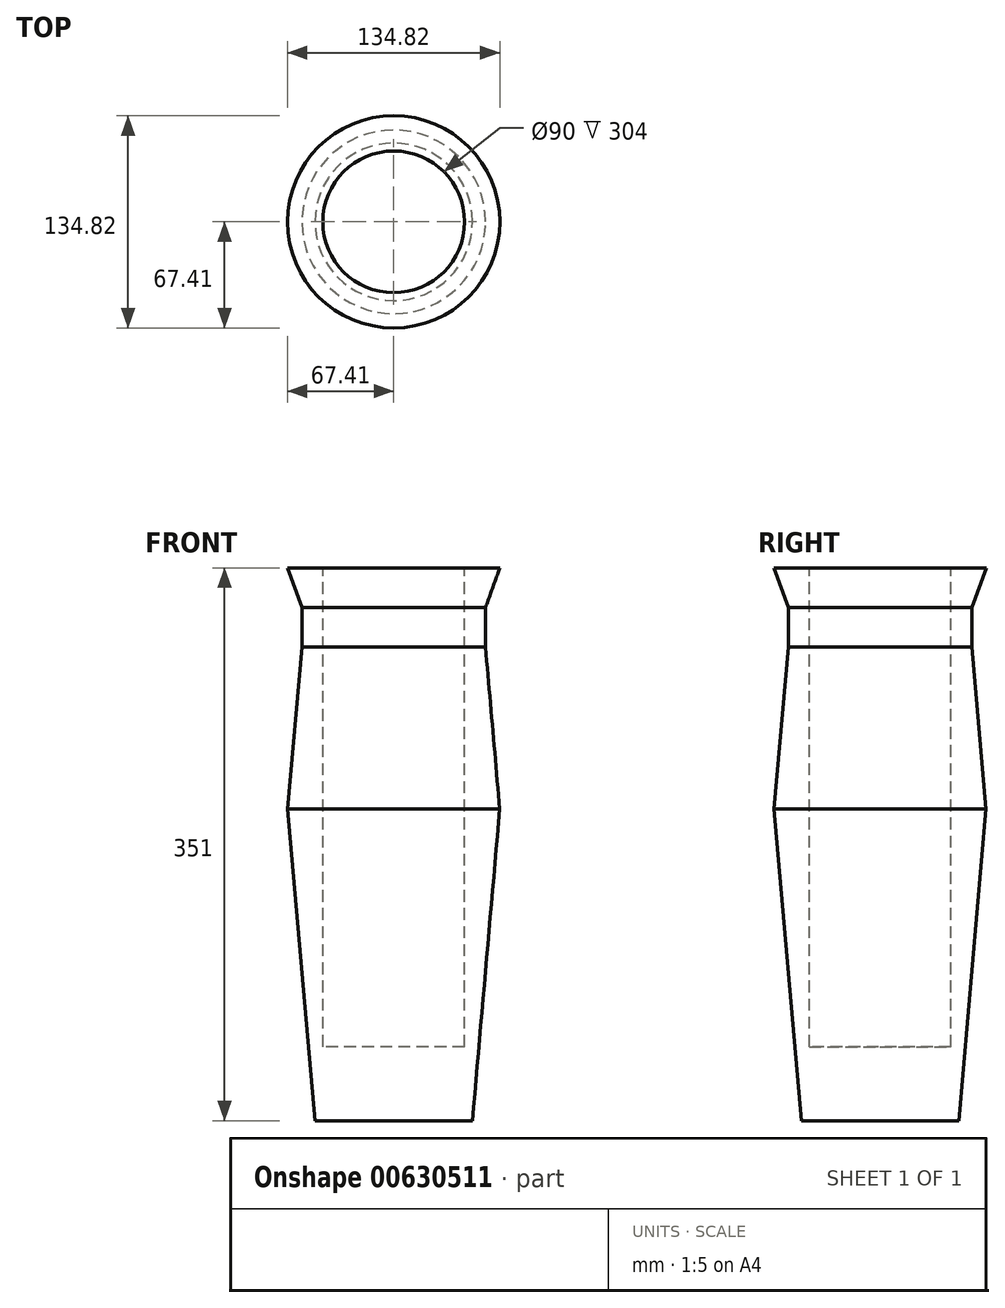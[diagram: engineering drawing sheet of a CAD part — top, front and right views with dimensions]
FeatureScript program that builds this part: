
annotation { "Feature Type Name" : "Feature", "Feature Type Description" : "" }
export const myFeature = defineFeature(function(context is Context, id is Id, definition is map)
    precondition{}
    {
        {
            var Q0;
            Q0=qCreatedBy(makeId("Top.planeOp"),FACE);
            var sketch = newSketch(context, id + "F0", { "sketchPlane" : qUnion([Q0])});
            skCircle(sketch, "E0", {"center": v(0, 0) * mm, "radius": 50 * mm});
            skSolve(sketch);
        }
        {
            var Q0;
            Q0=makeQuery(id+"F0.imprint","IMPRINT",FACE,{"disambiguationData":[TD([[makeQuery(id+"F0.imprint","IMPRINT",EDGE,{"derivedFrom":sQuery(id+"F0.wireOp",EDGE,"E0")}),1.0]])]});
            extrude(context, id + "F1", {"entities" : qUnion([Q0]), "depth" : 198 * mm, "offsetDistance" : 25 * mm, "hasDraft" : true, "draftAngle" : 5 * degree});
        }
        {
            var Q0;
            Q0=makeQuery(id+"F1.opExtrude","CAP_FACE",FACE,{"disambiguationData":[OSD([sQuery(id+"F0.wireOp",EDGE,"E0")])],"isStart":false});
            extrude(context, id + "F2", {"entities" : qUnion([Q0]), "operationType" : NewBodyOperationType.ADD, "depth" : 103 * mm, "offsetDistance" : 25 * mm, "hasDraft" : true, "draftAngle" : 5 * degree, "draftPullDirection" : true});
        }
        {
            var Q0;
            Q0=makeQuery(id+"F2.opExtrude","CAP_FACE",FACE,{"disambiguationData":[OSD([sQuery(id+"F0.wireOp",EDGE,"E0")])],"isStart":false});
            extrude(context, id + "F3", {"entities" : qUnion([Q0]), "operationType" : NewBodyOperationType.ADD, "depth" : 25 * mm, "offsetDistance" : 25 * mm});
        }
        {
            var Q0;
            Q0=makeQuery(id+"F3.opExtrude","CAP_FACE",FACE,{"disambiguationData":[OSD([sQuery(id+"F0.wireOp",EDGE,"E0")])],"isStart":false});
            extrude(context, id + "F4", {"entities" : qUnion([Q0]), "operationType" : NewBodyOperationType.ADD, "depth" : 25 * mm, "offsetDistance" : 25 * mm, "hasDraft" : true, "draftAngle" : 20 * degree});
        }
        {
            var Q0;
            Q0=makeQuery(id+"F4.opExtrude","CAP_FACE",FACE,{"disambiguationData":[OSD([sQuery(id+"F0.wireOp",EDGE,"E0")])],"isStart":false});
            var sketch = newSketch(context, id + "F5", { "sketchPlane" : qUnion([Q0])});
            skCircle(sketch, "E1", {"center": v(0, 0) * mm, "radius": 45 * mm});
            skSolve(sketch);
        }
        {
            var Q0;
            Q0 = qSketchRegion(id + "F5", true);
            extrude(context, id + "F6", {"entities" : qUnion([Q0]), "operationType" : NewBodyOperationType.REMOVE, "oppositeDirection" : true, "depth" : 304 * mm, "offsetDistance" : 25 * mm});
        }
    });
